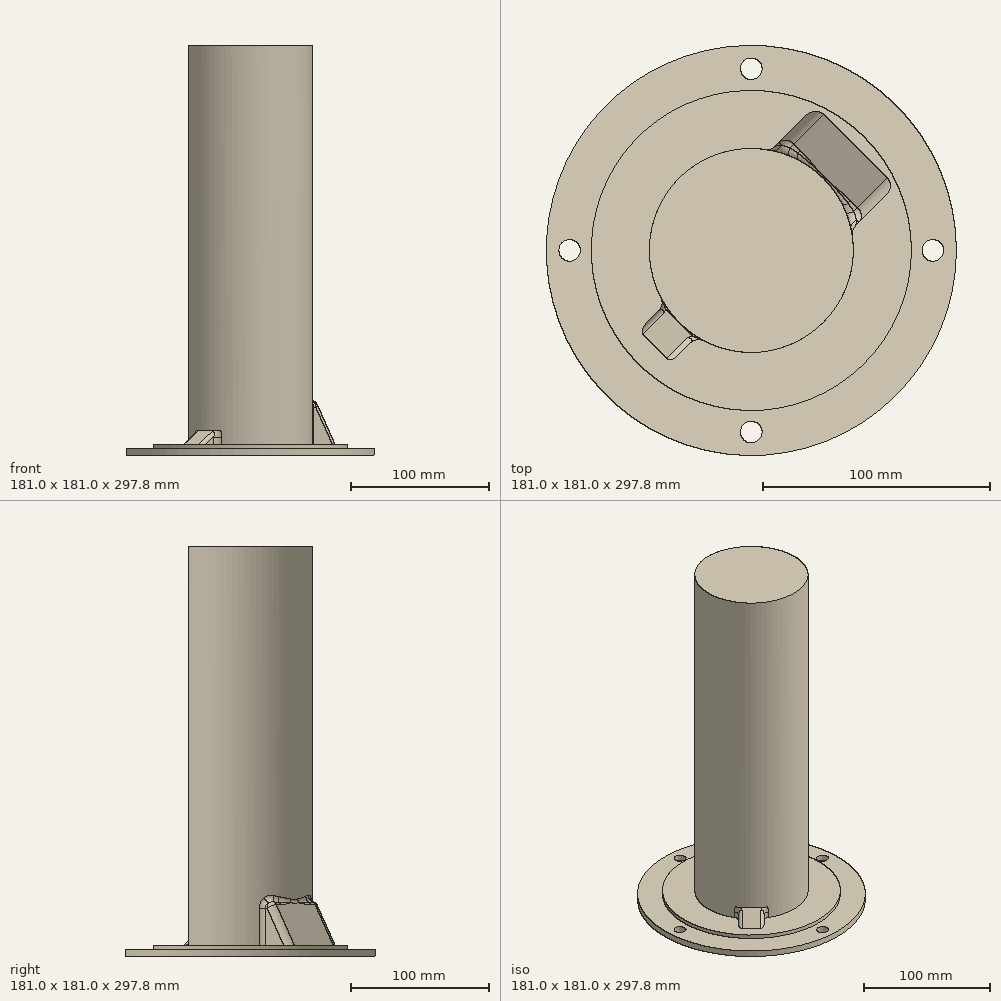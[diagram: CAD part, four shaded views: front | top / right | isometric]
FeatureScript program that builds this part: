
annotation { "Feature Type Name" : "Feature", "Feature Type Description" : "" }
export const myFeature = defineFeature(function(context is Context, id is Id, definition is map)
    precondition{}
    {
        {
            var Q0;
            Q0=qCreatedBy(makeId("Front.planeOp"),FACE);
            var sketch = newSketch(context, id + "F0", { "sketchPlane" : qUnion([Q0])});
            skLineSegment(sketch, "E0", {"start": v(0, 0) * mm, "end": v(90.49, 0) * mm});
            skLineSegment(sketch, "E1", {"start": v(90.49, 0) * mm, "end": v(90.49, 5.08) * mm});
            skLineSegment(sketch, "E2", {"start": v(90.49, 5.08) * mm, "end": v(70.64, 5.08) * mm});
            skLineSegment(sketch, "E3", {"start": v(70.64, 5.08) * mm, "end": v(70.64, 8.25) * mm});
            skLineSegment(sketch, "E4", {"start": v(70.64, 8.25) * mm, "end": v(45, 8.25) * mm});
            skLineSegment(sketch, "E5", {"start": v(45, 8.25) * mm, "end": v(0, 8.25) * mm});
            skLineSegment(sketch, "E6", {"start": v(0, 8.25) * mm, "end": v(0, 0) * mm});
            skSolve(sketch);
        }
        {
            var Q0;
            Q0 = qSketchRegion(id + "F0", true);
            var Q1;
            Q1=sQuery(id+"F0.wireOp",EDGE,"E6");
            revolve(context, id + "F1", {"entities" : qUnion([Q0]), "axis" : qUnion([Q1]), "revolveType" : RevolveType.FULL});
        }
        {
            var Q0;
            Q0=makeQuery(id+"F1.opRevolve","SWEPT_FACE",FACE,{"disambiguationData":[OSD([sQuery(id+"F0.wireOp",EDGE,"E0")])]});
            var sketch = newSketch(context, id + "F2", { "sketchPlane" : qUnion([Q0])});
            skCircle(sketch, "E7", {"center": v(-80.17, 0) * mm, "radius": 4.76 * mm});
            skCircle(sketch, "E8", {"center": v(0, 80.17) * mm, "radius": 4.76 * mm});
            skCircle(sketch, "E9", {"center": v(80.17, 0) * mm, "radius": 4.76 * mm});
            skCircle(sketch, "E10", {"center": v(0, -80.17) * mm, "radius": 4.76 * mm});
            skSolve(sketch);
        }
        {
            var Q0;
            Q0 = qSketchRegion(id + "F2", true);
            extrude(context, id + "F3", {"entities" : qUnion([Q0]), "operationType" : NewBodyOperationType.REMOVE, "oppositeDirection" : true, "depth" : 25.4 * mm, "offsetDistance" : 25.4 * mm});
        }
        {
            var Q0;
            Q0=qCreatedBy(makeId("Right.planeOp"),FACE);
            var Q1;
            Q1=qCreatedBy(makeId("Front.planeOp"),FACE);
            cPlane(context, id + "F4", {"entities" : qUnion([Q0, Q1]), "cplaneType" : CPlaneType.MID_PLANE, "offset" : 25.4 * mm, "width" : 152.4 * mm, "height" : 152.4 * mm});
        }
        {
            var Q0;
            Q0=qCreatedBy(id+"F4.planeOp",FACE);
            var sketch = newSketch(context, id + "F5", { "sketchPlane" : qUnion([Q0])});
            skLineSegment(sketch, "E11.bottom", {"start": v(25, 0) * mm, "end": v(-25, 0) * mm});
            skLineSegment(sketch, "E11.top", {"start": v(25, 40) * mm, "end": v(-25, 40) * mm});
            skLineSegment(sketch, "E11.left", {"start": v(25, 0) * mm, "end": v(25, 40) * mm});
            skLineSegment(sketch, "E11.right", {"start": v(-25, 0) * mm, "end": v(-25, 40) * mm});
            skSolve(sketch);
        }
        {
            var Q0;
            Q0=makeQuery(id+"F5.imprint","IMPRINT",FACE,{"disambiguationData":[TD([[makeQuery(id+"F5.imprint","IMPRINT",EDGE,{"derivedFrom":sQuery(id+"F5.wireOp",EDGE,"E11.bottom")}),-1.0]])]});
            extrude(context, id + "F6", {"entities" : qUnion([Q0]), "operationType" : NewBodyOperationType.ADD, "depth" : 45 * mm, "offsetDistance" : 25.4 * mm});
        }
        {
            var Q0;
            Q0=makeQuery(id+"F6.opExtrude","SWEPT_FACE",FACE,{"disambiguationData":[OSD([sQuery(id+"F5.wireOp",EDGE,"E11.left")])]});
            var sketch = newSketch(context, id + "F7", { "sketchPlane" : qUnion([Q0])});
            skLineSegment(sketch, "E12", {"start": v(-45, 40) * mm, "end": v(-45, 8.25) * mm});
            skLineSegment(sketch, "E13", {"start": v(-45, 8.25) * mm, "end": v(-65, 8.25) * mm});
            skLineSegment(sketch, "E14", {"start": v(-65, 8.25) * mm, "end": v(-45, 40) * mm});
            skSolve(sketch);
        }
        {
            var Q0;
            Q0=makeQuery(id+"F7.imprint","IMPRINT",FACE,{"disambiguationData":[TD([[makeQuery(id+"F7.imprint","IMPRINT",EDGE,{"derivedFrom":sQuery(id+"F7.wireOp",EDGE,"E12")}),1.0]])]});
            extrude(context, id + "F8", {"entities" : qUnion([Q0]), "operationType" : NewBodyOperationType.ADD, "oppositeDirection" : true, "depth" : 50 * mm, "offsetDistance" : 25.4 * mm});
        }
        {
            var Q0;
            Q0=makeQuery(id+"F6.opExtrude","CAP_FACE",FACE,{"disambiguationData":[OSD([sQuery(id+"F5.wireOp",EDGE,"E11.bottom"),sQuery(id+"F5.wireOp",EDGE,"E11.top"),sQuery(id+"F5.wireOp",EDGE,"E11.left"),sQuery(id+"F5.wireOp",EDGE,"E11.right")])],"isStart":true});
            var sketch = newSketch(context, id + "F9", { "sketchPlane" : qUnion([Q0])});
            skLineSegment(sketch, "E15.bottom", {"start": v(-10, 8.25) * mm, "end": v(10, 8.25) * mm});
            skLineSegment(sketch, "E16", {"start": v(10, 8.25) * mm, "end": v(10, 18.25) * mm});
            skLineSegment(sketch, "E17", {"start": v(10, 18.25) * mm, "end": v(-10, 18.25) * mm});
            skLineSegment(sketch, "E18", {"start": v(-10, 18.25) * mm, "end": v(-10, 8.25) * mm});
            skSolve(sketch);
        }
        {
            var Q0;
            Q0 = qSketchRegion(id + "F9", true);
            extrude(context, id + "F10", {"entities" : qUnion([Q0]), "operationType" : NewBodyOperationType.ADD, "depth" : 45 * mm, "offsetDistance" : 25.4 * mm});
        }
        {
            var Q0;
            Q0=makeQuery(id+"F10.opExtrude","SWEPT_FACE",FACE,{"disambiguationData":[OSD([sQuery(id+"F9.wireOp",EDGE,"E16")])]});
            var sketch = newSketch(context, id + "F11", { "sketchPlane" : qUnion([Q0])});
            skLineSegment(sketch, "E19", {"start": v(-45, 8.25) * mm, "end": v(-45, 18.25) * mm});
            skLineSegment(sketch, "E20", {"start": v(-45, 18.26) * mm, "end": v(-60, 8.26) * mm});
            skLineSegment(sketch, "E21", {"start": v(-60, 8.25) * mm, "end": v(-45, 8.25) * mm});
            skSolve(sketch);
        }
        {
            var Q0;
            Q0=makeQuery(id+"F11.imprint","IMPRINT",FACE,{"disambiguationData":[TD([[makeQuery(id+"F11.imprint","IMPRINT",EDGE,{"derivedFrom":sQuery(id+"F11.wireOp",EDGE,"E19")}),1.0]])]});
            extrude(context, id + "F12", {"entities" : qUnion([Q0]), "operationType" : NewBodyOperationType.ADD, "oppositeDirection" : true, "depth" : 20 * mm, "offsetDistance" : 25.4 * mm});
        }
        {
            var Q0;
            Q0=makeQuery(id+"F1.opRevolve","SWEPT_FACE",FACE,{"disambiguationData":[OSD([sQuery(id+"F0.wireOp",EDGE,"E4"),sQuery(id+"F0.wireOp",EDGE,"E5")])]});
            var sketch = newSketch(context, id + "F13", { "sketchPlane" : qUnion([Q0])});
            skCircle(sketch, "E22", {"center": v(0, 0) * mm, "radius": 45 * mm});
            skSolve(sketch);
        }
        {
            var Q0;
            Q0 = qSketchRegion(id + "F13", true);
            extrude(context, id + "F14", {"entities" : qUnion([Q0]), "operationType" : NewBodyOperationType.ADD, "depth" : 289.56 * mm, "offsetDistance" : 25.4 * mm});
        }
        {
            var Q0;
            Q0=makeQuery(id+"F8.opExtrude","CAP_EDGE",EDGE,{"disambiguationData":[OSD([sQuery(id+"F7.wireOp",EDGE,"E14")])],"isStart":false});
            var Q1;
            {var subQ0=sQuery(id+"F7.wireOp",EDGE,"E14");var subQ1=sQuery(id+"F7.wireOp",EDGE,"E12");var subQ2=sQuery(id+"F5.wireOp",EDGE,"E11.top");Q1=makeQuery(id+"F14.boolean.opBoolean","SPLIT",EDGE,{"disambiguationData":[TD([makeQuery(id+"F6.opExtrude","SWEPT_FACE",FACE,{"disambiguationData":[OSD([sQuery(id+"F5.wireOp",EDGE,"E11.right")])]})])],"derivedFrom":makeQuery(id+"F8.boolean.opBoolean","MERGE",EDGE,{"derivedFrom":[makeQuery(id+"F6.opExtrude","CAP_EDGE",EDGE,{"disambiguationData":[OSD([subQ2])],"isStart":false}),makeQuery(id+"F8.opExtrude","SWEPT_EDGE",EDGE,{"disambiguationData":[OSD([subQ2,sQuery(id+"F5.wireOp",EDGE,"E11.left"),subQ1,subQ0])]})]})});}
            var Q2;
            Q2=makeQuery(id+"F8.opExtrude","CAP_EDGE",EDGE,{"disambiguationData":[OSD([sQuery(id+"F7.wireOp",EDGE,"E14")])],"isStart":true});
            var Q3;
            Q3=makeQuery(id+"F6.opExtrude","SWEPT_EDGE",EDGE,{"disambiguationData":[OSD([sQuery(id+"F5.wireOp",EDGE,"E11.top"),sQuery(id+"F5.wireOp",EDGE,"E11.left")])]});
            var Q4;
            Q4=makeQuery(id+"F6.opExtrude","SWEPT_EDGE",EDGE,{"disambiguationData":[OSD([sQuery(id+"F5.wireOp",EDGE,"E11.top"),sQuery(id+"F5.wireOp",EDGE,"E11.right")])]});
            fillet(context, id + "F15", {"entities" : qUnion([Q0, Q1, Q2, Q3, Q4]), "radius" : 5.08 * mm, "tangentPropagation" : true, "allowEdgeOverflow" : false});
        }
        {
            var Q0;
            Q0=makeQuery(id+"F8.boolean.opBoolean","MERGE",EDGE,{"derivedFrom":[makeQuery(id+"F6.boolean.opBoolean","INTERSECT",EDGE,{"derivedFrom":[makeQuery(id+"F1.opRevolve","SWEPT_FACE",FACE,{"disambiguationData":[OSD([sQuery(id+"F0.wireOp",EDGE,"E4"),sQuery(id+"F0.wireOp",EDGE,"E5")])]}),makeQuery(id+"F6.opExtrude","SWEPT_FACE",FACE,{"disambiguationData":[OSD([sQuery(id+"F5.wireOp",EDGE,"E11.left")])]})]}),makeQuery(id+"F8.opExtrude","CAP_EDGE",EDGE,{"disambiguationData":[OSD([sQuery(id+"F7.wireOp",EDGE,"E13")])],"isStart":true})]});
            var Q1;
            Q1=makeQuery(id+"F14.boolean.opBoolean","INTERSECT",EDGE,{"derivedFrom":[makeQuery(id+"F8.boolean.opBoolean","MERGE",FACE,{"derivedFrom":[makeQuery(id+"F6.opExtrude","SWEPT_FACE",FACE,{"disambiguationData":[OSD([sQuery(id+"F5.wireOp",EDGE,"E11.left")])]}),makeQuery(id+"F8.opExtrude","CAP_FACE",FACE,{"disambiguationData":[OSD([sQuery(id+"F7.wireOp",EDGE,"E12"),sQuery(id+"F7.wireOp",EDGE,"E13"),sQuery(id+"F7.wireOp",EDGE,"E14")])],"isStart":true})]}),makeQuery(id+"F14.opExtrude","SWEPT_FACE",FACE,{"disambiguationData":[OSD([sQuery(id+"F13.wireOp",EDGE,"E22")])]})]});
            fillet(context, id + "F16", {"entities" : qUnion([Q0, Q1]), "radius" : 5.08 * mm, "tangentPropagation" : true, "allowEdgeOverflow" : false});
        }
        {
            var Q0;
            Q0=makeQuery(id+"F12.opExtrude","CAP_EDGE",EDGE,{"disambiguationData":[OSD([sQuery(id+"F11.wireOp",EDGE,"E20")])],"isStart":true});
            var Q1;
            Q1=makeQuery(id+"F12.opExtrude","SWEPT_EDGE",EDGE,{"disambiguationData":[OSD([sQuery(id+"F11.wireOp",EDGE,"E20"),sQuery(id+"F11.wireOp",EDGE,"E21")])]});
            var Q2;
            Q2=makeQuery(id+"F12.opExtrude","CAP_EDGE",EDGE,{"disambiguationData":[OSD([sQuery(id+"F11.wireOp",EDGE,"E20")])],"isStart":false});
            fillet(context, id + "F17", {"entities" : qUnion([Q0, Q1, Q2]), "radius" : 2.54 * mm, "tangentPropagation" : true, "allowEdgeOverflow" : false});
        }
        {
            var Q0;
            Q0=makeQuery(id+"F14.boolean.opBoolean","INTERSECT",EDGE,{"derivedFrom":[makeQuery(id+"F12.boolean.opBoolean","MERGE",FACE,{"derivedFrom":[makeQuery(id+"F10.opExtrude","SWEPT_FACE",FACE,{"disambiguationData":[OSD([sQuery(id+"F9.wireOp",EDGE,"E16")])]}),makeQuery(id+"F12.opExtrude","CAP_FACE",FACE,{"disambiguationData":[OSD([sQuery(id+"F11.wireOp",EDGE,"E19"),sQuery(id+"F11.wireOp",EDGE,"E20"),sQuery(id+"F11.wireOp",EDGE,"E21")])],"isStart":true})]}),makeQuery(id+"F14.opExtrude","SWEPT_FACE",FACE,{"disambiguationData":[OSD([sQuery(id+"F13.wireOp",EDGE,"E22")])]})]});
            var Q1;
            Q1=makeQuery(id+"F14.boolean.opBoolean","INTERSECT",EDGE,{"derivedFrom":[makeQuery(id+"F12.boolean.opBoolean","MERGE",FACE,{"derivedFrom":[makeQuery(id+"F10.opExtrude","SWEPT_FACE",FACE,{"disambiguationData":[OSD([sQuery(id+"F9.wireOp",EDGE,"E18")])]}),makeQuery(id+"F12.opExtrude","CAP_FACE",FACE,{"disambiguationData":[OSD([sQuery(id+"F11.wireOp",EDGE,"E19"),sQuery(id+"F11.wireOp",EDGE,"E20"),sQuery(id+"F11.wireOp",EDGE,"E21")])],"isStart":false})]}),makeQuery(id+"F14.opExtrude","SWEPT_FACE",FACE,{"disambiguationData":[OSD([sQuery(id+"F13.wireOp",EDGE,"E22")])]})]});
            fillet(context, id + "F18", {"entities" : qUnion([Q0, Q1]), "radius" : 5.08 * mm, "tangentPropagation" : true, "allowEdgeOverflow" : false});
        }
    });
